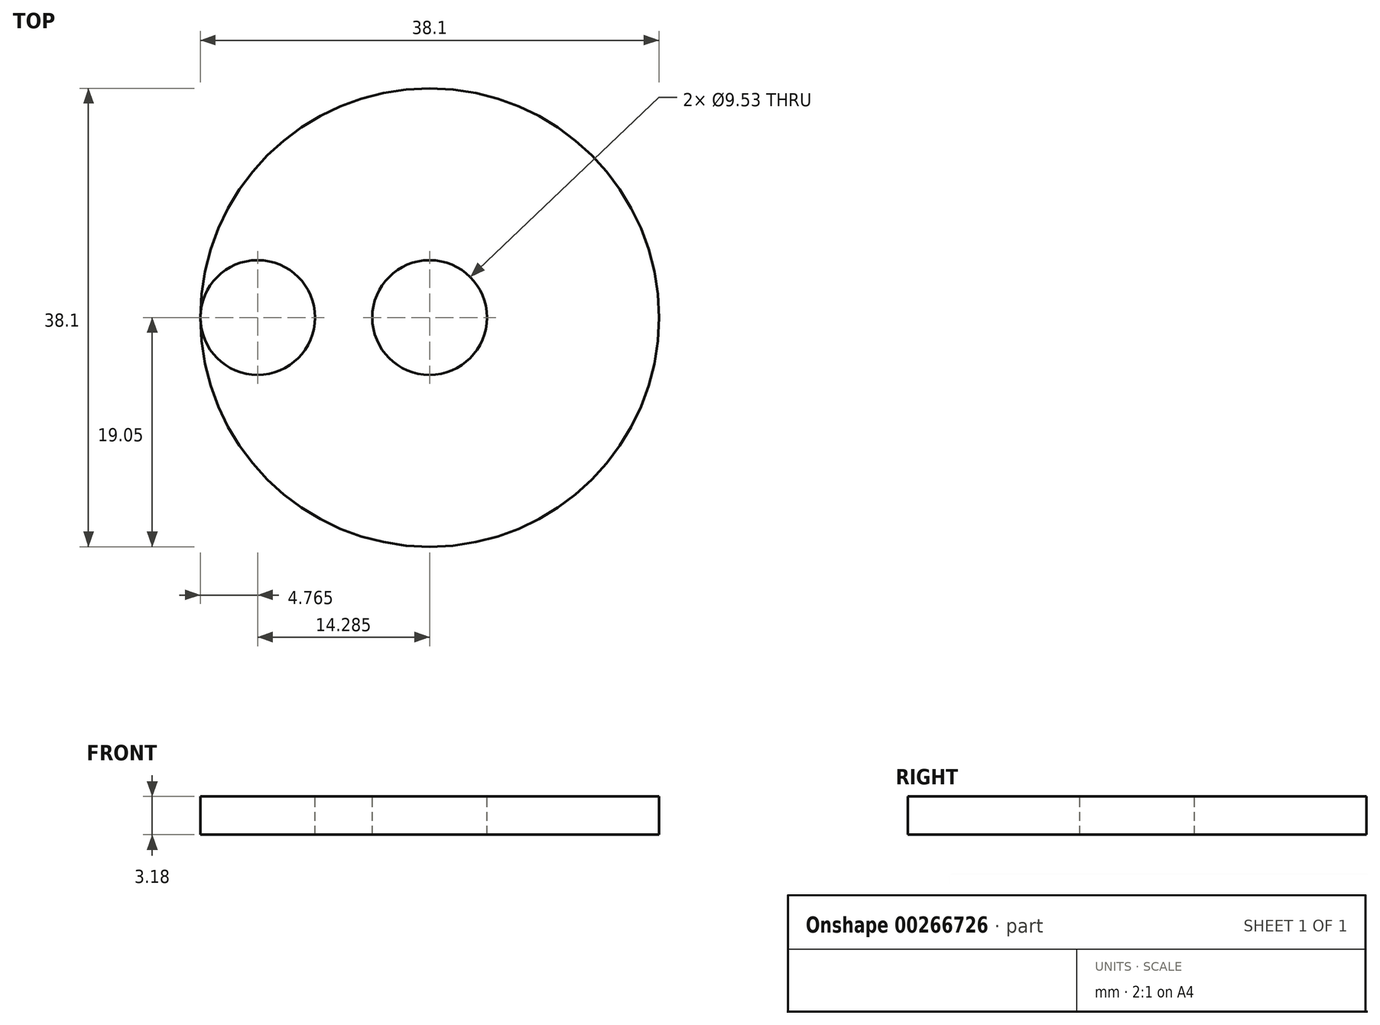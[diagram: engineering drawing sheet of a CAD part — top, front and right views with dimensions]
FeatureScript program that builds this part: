
annotation { "Feature Type Name" : "Feature", "Feature Type Description" : "" }
export const myFeature = defineFeature(function(context is Context, id is Id, definition is map)
    precondition{}
    {
        {
            var Q0;
            Q0=qCreatedBy(makeId("Top.planeOp"),FACE);
            var sketch = newSketch(context, id + "F0", { "sketchPlane" : qUnion([Q0])});
            skCircle(sketch, "E0", {"center": v(0, 0) * mm, "radius": 19.05 * mm});
            skSolve(sketch);
        }
        {
            var Q0;
            Q0 = qSketchRegion(id + "F0", true);
            extrude(context, id + "F1", {"entities" : qUnion([Q0]), "depth" : 3.17 * mm});
        }
        {
            var Q0;
            Q0=makeQuery(id+"F1.opExtrude","CAP_FACE",FACE,{"disambiguationData":[OSD([sQuery(id+"F0.wireOp",EDGE,"E0")])],"isStart":false});
            var sketch = newSketch(context, id + "F2", { "sketchPlane" : qUnion([Q0])});
            skPoint(sketch, "E1", {"position": v(0, 0) * mm});
            skCircle(sketch, "E2", {"center": v(-14.28, 0) * mm, "radius": 4.76 * mm});
            skCircle(sketch, "E3", {"center": v(0, 0) * mm, "radius": 4.76 * mm});
            skSolve(sketch);
        }
        {
            var Q0;
            Q0=makeQuery(id+"F2.imprint","IMPRINT",FACE,{"disambiguationData":[TD([[makeQuery(id+"F2.imprint","IMPRINT",EDGE,{"derivedFrom":sQuery(id+"F2.wireOp",EDGE,"E2")}),1.0]])]});
            var Q1;
            Q1=makeQuery(id+"F2.imprint","IMPRINT",FACE,{"disambiguationData":[TD([[makeQuery(id+"F2.imprint","IMPRINT",EDGE,{"derivedFrom":sQuery(id+"F2.wireOp",EDGE,"E3")}),1.0]])]});
            extrude(context, id + "F3", {"entities" : qUnion([Q0, Q1]), "operationType" : NewBodyOperationType.REMOVE, "oppositeDirection" : true, "depth" : 9.84 * mm});
        }
    });
